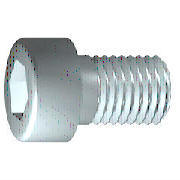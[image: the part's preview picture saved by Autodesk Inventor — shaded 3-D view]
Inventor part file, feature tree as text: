
AUTODESK INVENTOR PART (.ipt)
format: ipt  version: 2020 (Build 240168000, 168)  size: 193,536 bytes
history: native  units: mm (DEFAULTED — no unit token found)
features: sketch x2, other x1, extrude x1, plane x1, fillet x1
ambient origin geometry x7: Origin, YZ Plane, XY Plane, X Axis, Y Axis, Z Axis, Center Point
bodies: Solid1 (feature_tree)
feature tree (6):
  other  "Bryła"
  extrude  "Szczelina"  Depth=13.9mm
  plane  "Work Plane1"
  fillet  "Fillet2"  Radius=0.429515mm
  sketch  "Szkic1"
  sketch  "Szkic2"
